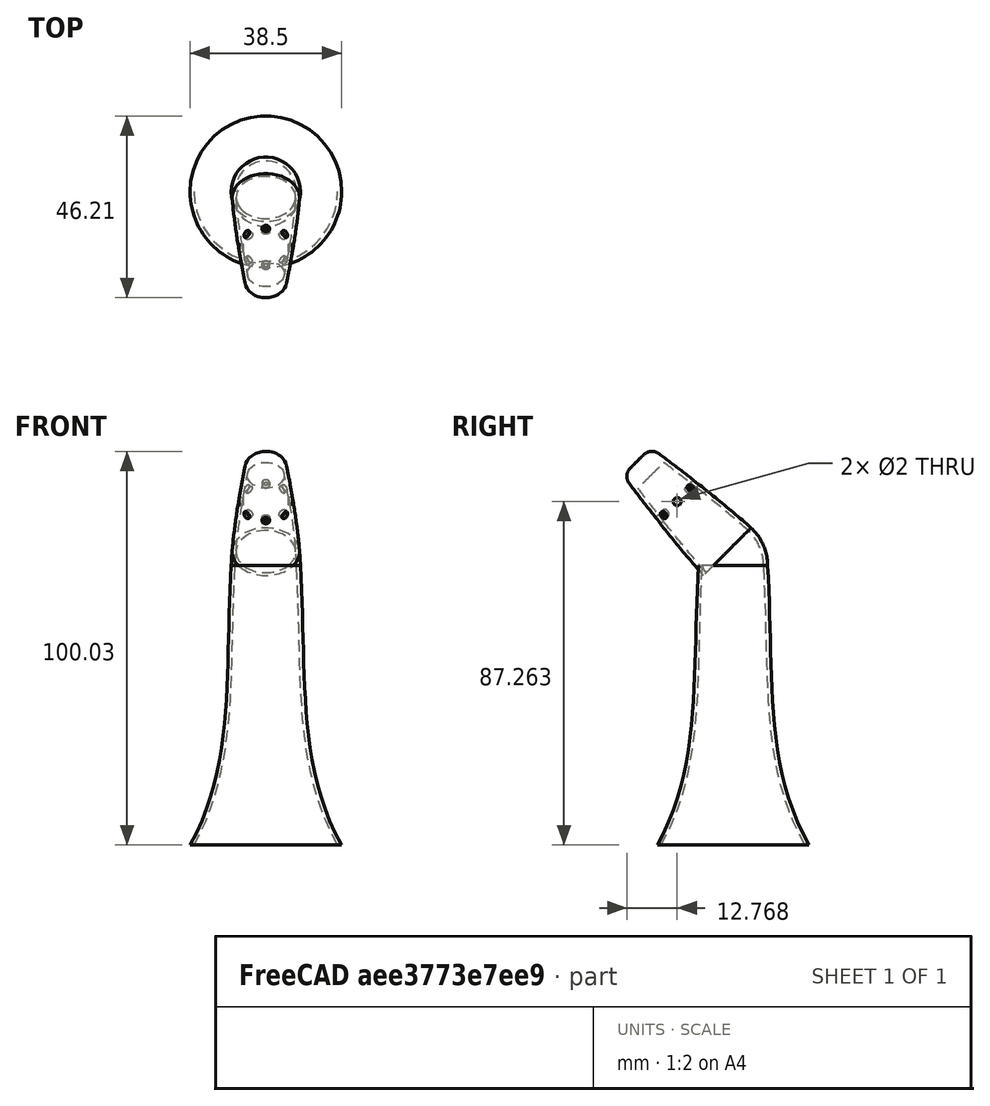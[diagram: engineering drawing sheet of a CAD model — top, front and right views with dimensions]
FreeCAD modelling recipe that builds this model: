
FCSTD DOCUMENT  (FreeCAD 1.1R20260414 (Git shallow))
Label: Waterpik
License: All rights reserved
LicenseURL: http://en.wikipedia.org/wiki/All_rights_reserved
objects: Sketcher::SketchObject×8, App::Point×2, Part::DatumPlane×2, Spreadsheet::Sheet×1, PartDesign::AdditivePipe×1, PartDesign::Pad×1, PartDesign::Pocket×1, PartDesign::PolarPattern×1, PartDesign::Fillet×1, PartDesign::Body×1, App::Part×1, Mesh::Feature×1
note: 31 computed .brp shape members not serialized (recipe doc carries the construction recipe); baked Part::Feature solids carry a one-line shape summary decoded from their .brp

FEATURE [App::Point] Origin001
  Role = Origin
FEATURE [App::Point] Origin003
  Role = Origin
FEATURE [Sketcher::SketchObject] Sketch  label="Sketch-Base1"
  ArcFitTolerance = 1e-06
  AttachmentOffset = pos=(0,0,-71) rot=(0,0,1;0rad)
  AttachmentSupport = -> [Origin002]
  ExternalTypes = [0]
  FullyConstrained = true
  MakeInternals = false
  MapMode = 5
  Placement = pos=(0,0,-71) rot=(0,0,1;0rad)
  _ExternalGeoVersion = 1
  expr: .AttachmentOffset.Base.z = -Spreadsheet.BaseH - Spreadsheet.NeckH
  expr: Constraints[2] = Spreadsheet.Thickness
  expr: Constraints[3] = Spreadsheet.Base1
  sketch-geometry (2):
    g0: Circle CenterX=0 CenterY=0 CenterZ=0 NormalX=0 NormalY=0 NormalZ=1 AngleXU=0 Radius=19.25
    g1: Circle CenterX=0 CenterY=0 CenterZ=0 NormalX=0 NormalY=0 NormalZ=1 AngleXU=0 Radius=18.25
  constraints (4):
    c: Coincident(g0,g-1)
    c: Coincident(g1,g0)
    c: Distance(g1,g0) = 1
    c: Diameter(g1) = 36.5
FEATURE [Sketcher::SketchObject] Sketch001  label="Sketch-Neck1"
  ArcFitTolerance = 1e-06
  AttachmentOffset = pos=(0,0,-33.5294) rot=(0,0,1;0rad)
  AttachmentSupport = -> [Origin002]
  ExternalTypes = [0]
  FullyConstrained = true
  MakeInternals = false
  MapMode = 5
  Placement = pos=(0,0,-33.5294) rot=(0,0,1;0rad)
  _ExternalGeoVersion = 1
  expr: .AttachmentOffset.Base.z = -Spreadsheet.NeckH / 1.7
  expr: Constraints[2] = Spreadsheet.Thickness
  expr: Constraints[3] = Spreadsheet.Neck1
  sketch-geometry (2):
    g0: Circle CenterX=0 CenterY=0 CenterZ=0 NormalX=0 NormalY=0 NormalZ=1 AngleXU=0 Radius=10
    g1: Circle CenterX=0 CenterY=0 CenterZ=0 NormalX=0 NormalY=0 NormalZ=1 AngleXU=0 Radius=9
  constraints (4):
    c: Coincident(g0,g-1)
    c: Coincident(g1,g0)
    c: Distance(g1,g0) = 1
    c: Diameter(g1) = 18
FEATURE [Sketcher::SketchObject] Sketch002  label="Sketch-Base2"
  ArcFitTolerance = 1e-06
  AttachmentOffset = pos=(0,0,-57) rot=(0,0,1;0rad)
  AttachmentSupport = -> [Origin002]
  ExternalTypes = [0]
  FullyConstrained = true
  MakeInternals = false
  MapMode = 5
  Placement = pos=(0,0,-57) rot=(0,0,1;0rad)
  _ExternalGeoVersion = 1
  expr: .AttachmentOffset.Base.z = -Spreadsheet.NeckH
  expr: Constraints[2] = Spreadsheet.Thickness
  expr: Constraints[3] = Spreadsheet.Base2
  sketch-geometry (2):
    g0: Circle CenterX=0 CenterY=0 CenterZ=0 NormalX=0 NormalY=0 NormalZ=1 AngleXU=0 Radius=13.5
    g1: Circle CenterX=0 CenterY=0 CenterZ=0 NormalX=0 NormalY=0 NormalZ=1 AngleXU=0 Radius=12.5
  constraints (4):
    c: Coincident(g0,g-1)
    c: Coincident(g1,g0)
    c: Distance(g1,g0) = 1
    c: Diameter(g1) = 25
FEATURE [Spreadsheet::Sheet] Spreadsheet
  cells = A2='Thickness; B2(Thickness)=1; A4='Base1; B4(Base1)=36.5; A5='Base2; B5(Base2)=25; A6='BaseH; B6(BaseH)=14; A8='Neck1; B8(Neck1)=18; A9='Neck2; B9(Neck2)=16; A10='NeckH; B10(NeckH)=57; A12='Beak1; B12(Beak1)=8; A13='BeakH; B13(BeakH)=36
FEATURE [Sketcher::SketchObject] Sketch007  label="Sketch-Neck2"
  ArcFitTolerance = 1e-06
  AttachmentOffset = pos=(0,0,-4) rot=(0,0,1;0rad)
  AttachmentSupport = -> [Origin002]
  ExternalTypes = [0]
  FullyConstrained = true
  MakeInternals = false
  MapMode = 5
  Placement = pos=(0,0,-4) rot=(0,0,1;0rad)
  _ExternalGeoVersion = 1
  expr: Constraints[0] = Spreadsheet.Thickness
  expr: Constraints[1] = Spreadsheet.Neck2
  sketch-geometry (2):
    g0: Circle CenterX=0 CenterY=0 CenterZ=0 NormalX=0 NormalY=0 NormalZ=1 AngleXU=0 Radius=9
    g1: Circle CenterX=0 CenterY=0 CenterZ=0 NormalX=0 NormalY=0 NormalZ=1 AngleXU=0 Radius=8
  constraints (4):
    c: Distance(g1,g0) = 1
    c: Diameter(g1) = 16
    c: Coincident(g1,g-1)
    c: Coincident(g0,g1)
FEATURE [Sketcher::SketchObject] Sketch009  label="Sketch-Path"
  ArcFitTolerance = 1e-06
  AttachmentSupport = -> [Origin002]
  ExternalTypes = [0]
  FullyConstrained = true
  MakeInternals = false
  MapMode = 5
  Placement = pos=(0,0,0) rot=(0.57735,0.57735,0.57735;2.0944rad)
  _ExternalGeoVersion = 1
  expr: Constraints[4] = Spreadsheet.NeckH + Spreadsheet.BaseH
  expr: Constraints[5] = Spreadsheet.BeakH
  sketch-geometry (3):
    g0: LineSegment StartX=0 StartY=-71 StartZ=0 EndX=0 EndY=0 EndZ=0
    g1: LineSegment StartX=-1.46447 StartY=3.53553 StartZ=0 EndX=-24.3992 EndY=26.4703 EndZ=0
    g2: ArcOfCircle CenterX=-5 CenterY=0 CenterZ=0 NormalX=0 NormalY=0 NormalZ=1 AngleXU=0 Radius=5 StartAngle=0 EndAngle=0.785398
  constraints (8):
    c: PointOnObject(g0,g-2)
    c: Tangent(g2,g1) = -1.5708
    c: Tangent(g2,g0) = -1.5708
    c: Radius(g2) = 5
    c: DistanceY(g0,g-1) = 71
    c: Distance(g-1,g1) = 36
    c: Angle(g-1,g1) = 2.35619
    c: Coincident(g0,g-1)
FEATURE [Part::DatumPlane] DatumPlane001  label="DatumPlane"
  AttachmentSupport = -> [Sketch009]
  MapMode = 7
  Placement = pos=(0,-24.3992,26.4703) rot=(0,0.92388,0.382683;3.14159rad)
FEATURE [Sketcher::SketchObject] Sketch006  label="Sketch-Beak1"
  ArcFitTolerance = 1e-06
  AttachmentSupport = -> [DatumPlane001]
  ExternalTypes = [0]
  FullyConstrained = true
  MakeInternals = false
  MapMode = 5
  Placement = pos=(0,-24.3992,26.4703) rot=(0,0.92388,0.382683;3.14159rad)
  _ExternalGeoVersion = 1
  expr: Constraints[0] = Spreadsheet.Thickness
  expr: Constraints[1] = Spreadsheet.Beak1
  sketch-geometry (2):
    g0: Circle CenterX=0 CenterY=0 CenterZ=0 NormalX=0 NormalY=0 NormalZ=1 AngleXU=0 Radius=5
    g1: Circle CenterX=0 CenterY=0 CenterZ=0 NormalX=0 NormalY=0 NormalZ=1 AngleXU=0 Radius=4
  constraints (4):
    c: Distance(g0,g1) = 1
    c: Diameter(g1) = 8
    c: Coincident(g0,g-1)
    c: Coincident(g1,g0)
FEATURE [Sketcher::SketchObject] Sketch010
  ArcFitTolerance = 1e-06
  AttachmentSupport = -> [DatumPlane001]
  ExternalTypes = [0]
  FullyConstrained = true
  MakeInternals = false
  MapMode = 5
  Placement = pos=(0,-24.3992,26.4703) rot=(0,0.92388,0.382683;3.14159rad)
  _ExternalGeoVersion = 1
  expr: Constraints[1] = Spreadsheet.Beak1 + 2 * Spreadsheet.Thickness
  sketch-geometry (1):
    g0: Circle CenterX=0 CenterY=0 CenterZ=0 NormalX=0 NormalY=0 NormalZ=1 AngleXU=0 Radius=5
  constraints (2):
    c: Coincident(g0,g-1)
    c: Diameter(g0) = 10
FEATURE [Part::DatumPlane] DatumPlane  label="DatumPlane001"
  AttachmentOffset = pos=(0,0,-18) rot=(0,1,0;1.5708rad)
  AttachmentSupport = -> [Sketch009]
  MapMode = 7
  Placement = pos=(0,-14.1924,16.2635) rot=(-0.357407,0.862856,0.357407;4.56541rad)
FEATURE [Sketcher::SketchObject] Sketch011
  ArcFitTolerance = 1e-06
  AttachmentSupport = -> [DatumPlane]
  ExternalTypes = [0]
  FullyConstrained = true
  MakeInternals = false
  MapMode = 5
  Placement = pos=(0,-14.1924,16.2635) rot=(0.357407,-0.862856,-0.357407;1.71777rad)
  _ExternalGeoVersion = 1
  sketch-geometry (1):
    g0: Circle CenterX=0 CenterY=0 CenterZ=0 NormalX=0 NormalY=0 NormalZ=1 AngleXU=0 Radius=1
  constraints (2):
    c: Coincident(g0,g-1)
    c: Diameter(g0) = 2
FEATURE [PartDesign::AdditivePipe] AdditivePipe
  AuxiliaryCurvilinear = true
  AuxiliarySpineTangent = false
  Binormal = (0,0,0)
  Mode = 0
  Profile = -> Sketch
  Sections = -> [Sketch002,Sketch001,Sketch007,Sketch006]
  Spine = -> Sketch009
  SpineTangent = false
  Suppressed = false
  Transformation = 1
  Transition = 0
FEATURE [PartDesign::Pad] Pad
  BaseFeature = -> AdditivePipe
  Direction = (0,0.707107,-0.707107)
  Length = 5
  Length2 = 10
  Profile = -> Sketch010
  ReferenceAxis = -> Sketch010 [N_Axis]
  SideType = 0
  Suppressed = false
  TaperAngle = 4
  Type = 0
  Type2 = 0
FEATURE [PartDesign::Pocket] Pocket
  BaseFeature = -> Pad
  Direction = (1,0,0)
  Length = 15
  Length2 = 5
  Profile = -> Sketch011
  ReferenceAxis = -> Sketch011 [N_Axis]
  SideType = 0
  Suppressed = false
  Type = 0
  Type2 = 0
FEATURE [PartDesign::PolarPattern] PolarPattern
  Angle = 360
  Axis = -> Sketch011 [H_Axis]
  BaseFeature = -> Pocket
  Mode = 0
  Occurrences = 8
  Offset = 120
  Originals = -> [Pocket]
  SpacingPattern = [0]
  Spacings = [-1,-1,-1,-1,-1,-1,-1]
  Suppressed = false
  TransformMode = 0
FEATURE [PartDesign::Fillet] Fillet
  Base = -> PolarPattern [Edge34,Edge22]
  BaseFeature = -> PolarPattern
  Radius = 3
  SupportTransform = false
  Suppressed = false
  UseAllEdges = false
FEATURE [PartDesign::Body] Body
  AllowCompound = true
  Group = -> [Sketch,Sketch002,Sketch001,Sketch007,Sketch006,Sketch009,DatumPlane001,Sketch010,DatumPlane,Sketch011,AdditivePipe,Pad,Pocket,PolarPattern,Fillet]
  Origin = -> Origin002
  Tip = -> Fillet
FEATURE [App::Part] Part
  Group = -> [Body]
  Origin = -> Origin
FEATURE [Mesh::Feature] Mesh  label="Fillet (Meshed)"
